# Revit family: IS_iLifeS_T4737_BIM_NL
name_source: partatom
category: Plumbing Fixtures
units: mm (PartAtom-declared; Revit-internal decimal feet)

## family parameters
Always vertical = No
Cut with Voids When Loaded = No
OmniClass Number = 23.45.05.21.11.11
OmniClass Title = Water Operated Water Closets
Part Type = Normal
Room Calculation Point = No
Round Connector Dimension = Use Diameter
Shared = No
Work Plane-Based = No

## types (1)
- T473701 - i.life S wrapover seat, Soft Close - White
    Accessories = https://www.idealstandard.nl
    Afmetingen = 43 x 412 x 361 mm
    AfstandsEenheid = Millimeter
    Afwerking = Weiß
    AreaUnits = millimetres
    Artikelnummer = T473701
    Artikelomschrijving = Ideal Standard i.life S Wickelsitz, kompakt, Softclose, leicht abnehmbarer Druckknopf, verstellbares Scharnier, weiß, im Karton, im Umkarton, EU-Palette
    AssetType = Fixed
    Auteur = Ideal Standard
    BIMObjectName = IS_IdealStandard_WC seats and covers_i.lifeS_T4737
    BIMobject category = Toilet Seats
    BIMobject category code = toilet-seats
    BIMobject main category = Sanitary
    BIMobject main category code = sanitary
    BarCode = 8014140491453
    Beschrijvinggarantie = Herstellergarantie
    BimObjectNaam = IS_IdealStandard_WC seats and covers_i.lifeS_T4737
    Brand = Ideal Standard
    Brand url = https://www.idealstandard.nl
    Breedte = 361.2409
    BrutoGewicht = 0
    Category = Sanitary
    Color = Weiß
    ConnectionType = Plumbing
    Cost = 0 $
    CurrencyUnit = €
    CurrentRevision = 1
    Date of publishing = 27/05/2022
    Description = Ideal Standard i.life S wrapover seat, compact, softclose close,  easy-take off push button, adjustable hinge, white, in carton box, in master box, EU pallet
    Diepte = 412 mm
    DurationUnit = Years
    DuurEenheid = Jahre
    Edition number = 1
    Eigenschappen = Wickelsitz, kompakt, Softclose, leicht abnehmbarer Druckknopf, verstellbares Scharnier, weiß, im Karton, im Umkarton, EU-Palette
    ElementType = Fixed
    ExpectedLife = 99
    Features = wrapover seat, compact, softclose close,  easy-take off push button, adjustable hinge, white, in carton box, in master box, EU pallet
    Finish = White
    GTIN code = https://8014140491453
    Garantieunits = Jahre
    Help = https://www.idealstandard.nl
    Hoogte = 42.6674593687058
    Hulp = https://www.idealstandard.nl
    IFC Classification = Sanitary Terminal
    IfcExportAs = IfcSanitaryTerminalType
    IfcExportType = TOILETPAN
    Installatieinstructies = https://www.idealstandard.nl
    Installation instructions = https://www.idealstandard.nl
    InstallationInstructions = https://www.idealstandard.nl
    IsAutomaticFlush = No
    Kleur = Weiß
    Lengte = 412 mm
    LinearUnits = Millimetres
    MainColor = White
    MaintenanceInformation = https://www.idealstandard.nl
    Manufacturer = Ideal Standard
    Manufacturer name = Ideal Standard
    ManufacturerURL = https://www.idealstandard.nl
    Materiaal = Harnstoff
    Material = Urea
    Material main = Urea
    Merk = Ideal Standard
    Model = T473701
    ModelNumber = T473701
    ModelReference = i.life S wrapover seat, Soft Close
    NBS Reference Code = 45-35-70/391
    NBS Reference Description = WC seats and covers
    Name = WC seats and covers_i.lifeS_T4737_IdealStandard
    NettWeight = 1.78
    Nettogewicht = 1.78
    NominalDepth = 412 mm
    NominalHeight = 43 mm
    NominalLength = 412 mm
    NominalWidth = 361 mm
    Normen = WC seats and covers_i.lifeS_T4737_IdealStandard
    OmniClass Code = 23-31 19 19 17
    OmniClass Description = Water Closet Seats
    OppervlakteEenheid = Millimeter
    PredefinedType = Sanitary
    Product Guid = 137dc4ac-32f2-4dc6-b4d9-2322e2ad38a9
    Product SKU = T4737
    Product certification = https://www.idealstandard.nl
    Product data url = https://bimobject.com
    Product family = I.life S
    Product group = Sanitary: Seats & Covers
    Product name = i.life S wrapover seat, Soft Close
    Product url = https://www.idealstandard.nl
    ProductInformation = https://www.idealstandard.nl
    Productinformatie = https://www.idealstandard.nl
    QR code = http://bimobject.com
    Referentie = i.life S wrapover seat, Soft Close
    ReplacementCost = 0
    Revisie = 1
    Shape = Sculpture
    Size = 43 x 412 x 361 mm
    Space = Internal
    SpareParts = https://www.idealstandard.nl
    Technical description = https://www.idealstandard.nl
    Telefoonnummer = 077 355 08 08
    Typeconnectie = Installation
    UNSPSC Code = 301815
    URL = https://www.idealstandard.nl
    Uniclass 2015 Code = Pr_40_20_93_95
    Uniclass 2015 Name = WC seats and covers
    Uniclass2015Beschrijving = WC seats and covers
    Uniclass2015Code = Pr_40_20_93_95
    Uniclass2015Referentie = Pr_40_20_93_95
    Uniclass2015Title = WC seats and covers
    Uniclass2015Version = v.25
    Urlproducent = https://www.idealstandard.nl
    ValutaEenheid = Euro
    Versie = 1
    Version = 1
    Vervangingskosten = 0
    VolumeUnits = Litres
    Volumeunits = Liter
    Vorm = geformt
    WRASURL = https://www.wrasapprovals.co.uk
    WarrantyDescription = manufacturer warranty
    WarrantyDurationUnit = years
    Wisselstukken = https://www.idealstandard.nl
    Youtube clip = https://www.youtube.com

## geometry (parser evidence)
native form markers: Sweep x2
no freeform markers — native parametric forms only
